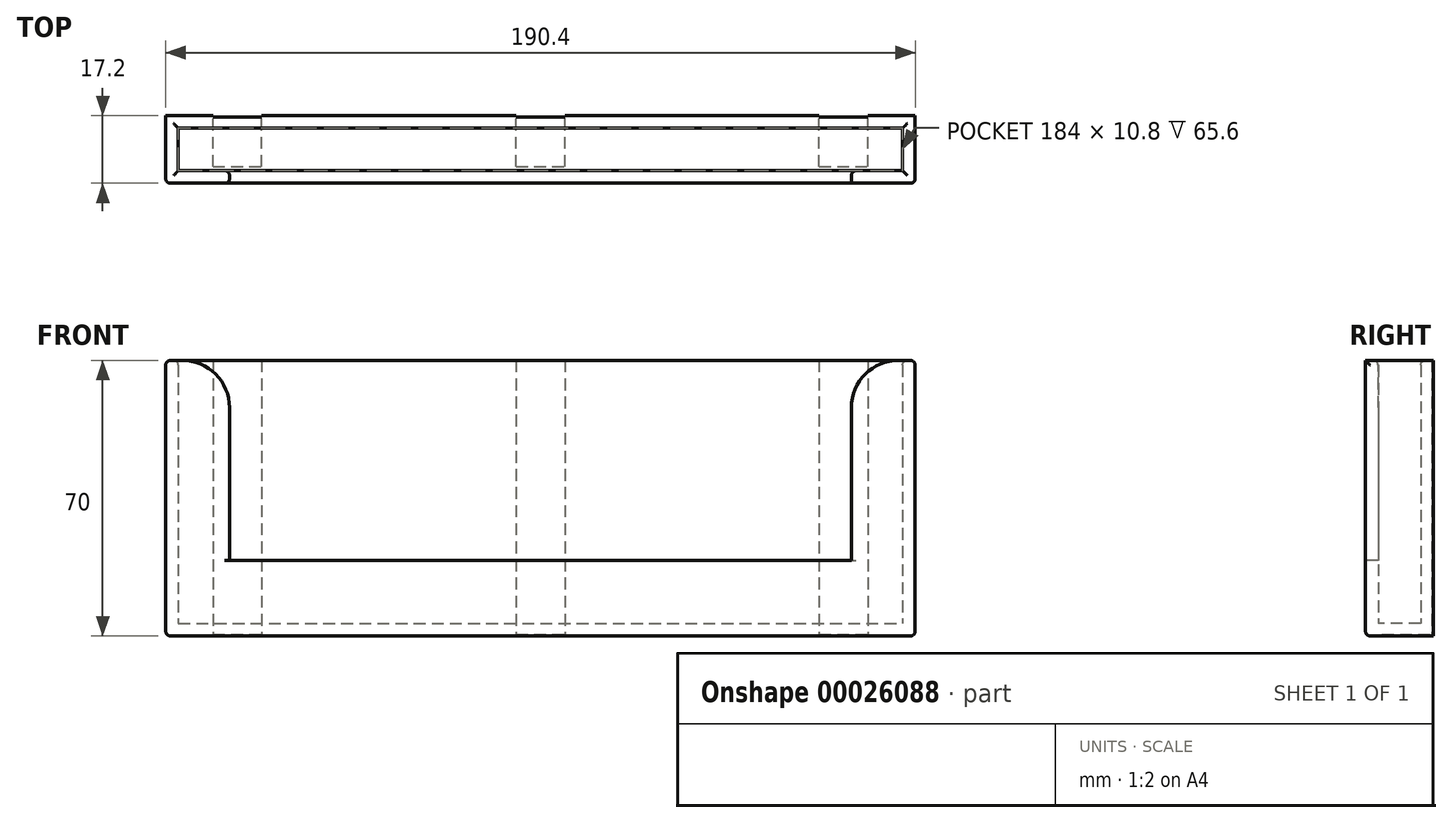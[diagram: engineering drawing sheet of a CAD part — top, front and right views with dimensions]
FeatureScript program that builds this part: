
annotation { "Feature Type Name" : "Feature", "Feature Type Description" : "" }
export const myFeature = defineFeature(function(context is Context, id is Id, definition is map)
    precondition{}
    {
        {
            var Q0;
            Q0=qCreatedBy(makeId("Top.planeOp"),FACE);
            var sketch = newSketch(context, id + "F0", { "sketchPlane" : qUnion([Q0])});
            skLineSegment(sketch, "E0.bottom", {"start": v(-78.63, 21.45) * mm, "end": v(105.37, 21.45) * mm});
            skLineSegment(sketch, "E0.top", {"start": v(-78.63, 10.65) * mm, "end": v(105.37, 10.65) * mm});
            skLineSegment(sketch, "E0.left", {"start": v(-78.63, 21.45) * mm, "end": v(-78.63, 10.65) * mm});
            skLineSegment(sketch, "E0.right", {"start": v(105.37, 21.45) * mm, "end": v(105.37, 10.65) * mm});
            skSolve(sketch);
        }
        {
            var Q0;
            Q0=makeQuery(id+"F0.imprint","IMPRINT",FACE,{"disambiguationData":[TD([[makeQuery(id+"F0.imprint","IMPRINT",EDGE,{"derivedFrom":sQuery(id+"F0.wireOp",EDGE,"E0.bottom")}),-1.0]])]});
            extrude(context, id + "F1", {"entities" : qUnion([Q0]), "depth" : 3.2 * mm});
        }
        {
            var Q0;
            Q0=qCreatedBy(makeId("Top.planeOp"),FACE);
            var sketch = newSketch(context, id + "F2", { "sketchPlane" : qUnion([Q0])});
            skLineSegment(sketch, "E1.0", {"start": v(-78.63, 10.65) * mm, "end": v(105.37, 10.65) * mm});
            skLineSegment(sketch, "E2.0", {"start": v(-78.63, 21.45) * mm, "end": v(-78.63, 10.65) * mm});
            skLineSegment(sketch, "E3.0", {"start": v(-78.63, 21.45) * mm, "end": v(105.37, 21.45) * mm});
            skLineSegment(sketch, "E4.0", {"start": v(105.37, 21.45) * mm, "end": v(105.37, 10.65) * mm});
            skLineSegment(sketch, "E5.0", {"start": v(-81.83, 7.45) * mm, "end": v(108.57, 7.45) * mm});
            skLineSegment(sketch, "E6.0", {"start": v(-81.83, 24.65) * mm, "end": v(108.57, 24.65) * mm});
            skLineSegment(sketch, "E7.0", {"start": v(-81.83, 24.65) * mm, "end": v(-81.83, 7.45) * mm});
            skLineSegment(sketch, "E8.0", {"start": v(108.57, 24.65) * mm, "end": v(108.57, 7.45) * mm});
            skSolve(sketch);
        }
        {
            var Q0;
            Q0=makeQuery(id+"F2.imprint","IMPRINT",FACE,{"disambiguationData":[TD([[makeQuery(id+"F2.imprint","IMPRINT",EDGE,{"derivedFrom":sQuery(id+"F2.wireOp",EDGE,"E1.0")}),-1.0]])]});
            extrude(context, id + "F3", {"entities" : qUnion([Q0]), "operationType" : NewBodyOperationType.ADD, "depth" : 70 * mm});
        }
        {
            var Q0;
            Q0=makeQuery(id+"F3.opExtrude","SWEPT_FACE",FACE,{"disambiguationData":[OSD([sQuery(id+"F2.wireOp",EDGE,"E5.0")])]});
            var sketch = newSketch(context, id + "F4", { "sketchPlane" : qUnion([Q0])});
            skLineSegment(sketch, "E9.0", {"start": v(-65.63, 19.2) * mm, "end": v(92.37, 19.2) * mm});
            skLineSegment(sketch, "E10.0", {"start": v(-65.63, 58) * mm, "end": v(-65.63, 19.2) * mm});
            skLineSegment(sketch, "E11.0", {"start": v(92.37, 58) * mm, "end": v(92.37, 19.2) * mm});
            skLineSegment(sketch, "E12.0", {"start": v(-81.83, 70) * mm, "end": v(-77.63, 70) * mm});
            skLineSegment(sketch, "E13.trimOffspring", {"start": v(104.37, 70) * mm, "end": v(108.57, 70) * mm});
            skPoint(sketch, "E14.visualSharp", {"position": v(-65.63, 70) * mm});
            skArc(sketch, "E14.filletArc", {"start": v(-65.63, 58) * mm, "mid": v(-69.15, 66.49) * mm, "end": v(-77.63, 70) * mm});
            skPoint(sketch, "E15.visualSharp", {"position": v(92.37, 70) * mm});
            skArc(sketch, "E15.filletArc", {"start": v(104.37, 70) * mm, "mid": v(95.88, 66.49) * mm, "end": v(92.37, 58) * mm});
            skSolve(sketch);
        }
        {
            var Q0;
            Q0=makeQuery(id+"F4.imprint","IMPRINT",FACE,{"disambiguationData":[TD([[makeQuery(id+"F4.imprint","IMPRINT",EDGE,{"derivedFrom":sQuery(id+"F4.wireOp",EDGE,"E9.0")}),1.0]])]});
            var Q1;
            Q1=makeQuery(id+"F3.opExtrude","SWEPT_FACE",FACE,{"disambiguationData":[OSD([sQuery(id+"F2.wireOp",EDGE,"E1.0")])]});
            extrude(context, id + "F5", {"entities" : qUnion([Q0]), "operationType" : NewBodyOperationType.REMOVE, "endBound" : BoundingType.UP_TO_SURFACE, "oppositeDirection" : true, "endBoundEntityFace" : qUnion([Q1]), "depth" : 25.4 * mm});
        }
        {
            var Q0;
            Q0=makeQuery(id+"F3.opExtrude","SWEPT_FACE",FACE,{"disambiguationData":[OSD([sQuery(id+"F2.wireOp",EDGE,"E6.0")])]});
            var sketch = newSketch(context, id + "F6", { "sketchPlane" : qUnion([Q0])});
            skLineSegment(sketch, "E16.0", {"start": v(-108.57, 70) * mm, "end": v(-108.57, 0) * mm});
            skLineSegment(sketch, "E17.0", {"start": v(81.83, 0) * mm, "end": v(-108.57, 0) * mm});
            skLineSegment(sketch, "E18.0", {"start": v(81.83, 70) * mm, "end": v(81.83, 0) * mm});
            skLineSegment(sketch, "E19.0", {"start": v(81.83, 70) * mm, "end": v(-108.57, 70) * mm});
            skLineSegment(sketch, "E20", {"start": v(-13.37, 70) * mm, "end": v(-13.37, 0) * mm, "construction": true});
            skLineSegment(sketch, "E21.0", {"start": v(-19.57, 70) * mm, "end": v(-19.57, 0) * mm});
            skLineSegment(sketch, "E22.0", {"start": v(-7.17, 70) * mm, "end": v(-7.17, 0) * mm});
            skLineSegment(sketch, "E23.0", {"start": v(-96.57, 70) * mm, "end": v(-96.57, 0) * mm});
            skLineSegment(sketch, "E24.0", {"start": v(-84.17, 70) * mm, "end": v(-84.17, 0) * mm});
            skLineSegment(sketch, "E25.0", {"start": v(69.83, 70) * mm, "end": v(69.83, 0) * mm});
            skLineSegment(sketch, "E26.0", {"start": v(57.43, 70) * mm, "end": v(57.43, 0) * mm});
            skSolve(sketch);
        }
        {
            var Q0;
            {var subQ0=sQuery(id+"F6.wireOp",EDGE,"E23.0");Q0=makeQuery(id+"F6.imprint","IMPRINT",FACE,{"disambiguationData":[TD([[makeQuery(id+"F6.imprint","IMPRINT",EDGE,{"derivedFrom":subQ0}),1.0]])]});}
            var Q1;
            {var subQ0=sQuery(id+"F6.wireOp",EDGE,"E21.0");Q1=makeQuery(id+"F6.imprint","IMPRINT",FACE,{"disambiguationData":[TD([[makeQuery(id+"F6.imprint","IMPRINT",EDGE,{"derivedFrom":subQ0}),1.0]])]});}
            var Q2;
            {var subQ0=sQuery(id+"F6.wireOp",EDGE,"E25.0");Q2=makeQuery(id+"F6.imprint","IMPRINT",FACE,{"disambiguationData":[TD([[makeQuery(id+"F6.imprint","IMPRINT",EDGE,{"derivedFrom":subQ0}),-1.0]])]});}
            extrude(context, id + "F7", {"entities" : qUnion([Q0, Q1, Q2]), "operationType" : NewBodyOperationType.REMOVE, "oppositeDirection" : true, "depth" : .4 * mm});
        }
        {
            var Q0;
            Q0=makeQuery(id+"F3.boolean.opBoolean","MERGE",FACE,{"derivedFrom":[makeQuery(id+"F1.opExtrude","CAP_FACE",FACE,{"disambiguationData":[OSD([sQuery(id+"F0.wireOp",EDGE,"E0.bottom"),sQuery(id+"F0.wireOp",EDGE,"E0.top"),sQuery(id+"F0.wireOp",EDGE,"E0.left"),sQuery(id+"F0.wireOp",EDGE,"E0.right")])],"isStart":true}),makeQuery(id+"F3.opExtrude","CAP_FACE",FACE,{"disambiguationData":[OSD([sQuery(id+"F2.wireOp",EDGE,"E1.0"),sQuery(id+"F2.wireOp",EDGE,"E2.0"),sQuery(id+"F2.wireOp",EDGE,"E3.0"),sQuery(id+"F2.wireOp",EDGE,"E4.0"),sQuery(id+"F2.wireOp",EDGE,"E5.0"),sQuery(id+"F2.wireOp",EDGE,"E6.0"),sQuery(id+"F2.wireOp",EDGE,"E7.0"),sQuery(id+"F2.wireOp",EDGE,"E8.0")])],"isStart":true})]});
            var sketch = newSketch(context, id + "F8", { "sketchPlane" : qUnion([Q0])});
            skLineSegment(sketch, "E27.0", {"start": v(96.57, -24.65) * mm, "end": v(108.57, -24.65) * mm, "construction": true});
            skLineSegment(sketch, "E28.0", {"start": v(108.57, -24.65) * mm, "end": v(108.57, -7.45) * mm, "construction": true});
            skLineSegment(sketch, "E29.0", {"start": v(84.17, -24.25) * mm, "end": v(96.57, -24.25) * mm});
            skLineSegment(sketch, "E30.0", {"start": v(96.57, -11.65) * mm, "end": v(96.57, -24.65) * mm});
            skLineSegment(sketch, "E31.0", {"start": v(84.17, -11.65) * mm, "end": v(84.17, -24.65) * mm});
            skLineSegment(sketch, "E32.0", {"start": v(19.57, -24.65) * mm, "end": v(84.17, -24.65) * mm, "construction": true});
            skLineSegment(sketch, "E33.0", {"start": v(19.57, -11.65) * mm, "end": v(19.57, -24.65) * mm});
            skLineSegment(sketch, "E34.0", {"start": v(7.17, -24.25) * mm, "end": v(19.57, -24.25) * mm});
            skLineSegment(sketch, "E35.0", {"start": v(7.17, -11.65) * mm, "end": v(7.17, -24.65) * mm});
            skLineSegment(sketch, "E36.0", {"start": v(-57.43, -24.65) * mm, "end": v(7.17, -24.65) * mm, "construction": true});
            skLineSegment(sketch, "E37.0", {"start": v(-57.43, -11.65) * mm, "end": v(-57.43, -24.65) * mm});
            skLineSegment(sketch, "E38.0", {"start": v(-69.83, -24.25) * mm, "end": v(-57.43, -24.25) * mm});
            skLineSegment(sketch, "E39.0", {"start": v(-69.83, -11.65) * mm, "end": v(-69.83, -24.65) * mm});
            skLineSegment(sketch, "E40.0", {"start": v(-81.83, -24.65) * mm, "end": v(-69.83, -24.65) * mm, "construction": true});
            skLineSegment(sketch, "E41.0", {"start": v(-81.83, -24.65) * mm, "end": v(-81.83, -7.45) * mm, "construction": true});
            skLineSegment(sketch, "E42.0", {"start": v(-69.83, -11.65) * mm, "end": v(-57.43, -11.65) * mm});
            skLineSegment(sketch, "E43.trimOffspring", {"start": v(84.17, -11.65) * mm, "end": v(96.57, -11.65) * mm});
            skLineSegment(sketch, "E44.trimOffspring", {"start": v(7.17, -11.65) * mm, "end": v(19.57, -11.65) * mm});
            skSolve(sketch);
        }
        {
            var Q0;
            {var subQ0=sQuery(id+"F8.wireOp",EDGE,"E34.0");Q0=makeQuery(id+"F8.imprint","IMPRINT",FACE,{"disambiguationData":[TD([[makeQuery(id+"F8.imprint","IMPRINT",EDGE,{"derivedFrom":subQ0}),1.0]])]});}
            var Q1;
            {var subQ0=sQuery(id+"F8.wireOp",EDGE,"E38.0");Q1=makeQuery(id+"F8.imprint","IMPRINT",FACE,{"disambiguationData":[TD([[makeQuery(id+"F8.imprint","IMPRINT",EDGE,{"derivedFrom":subQ0}),1.0]])]});}
            var Q2;
            {var subQ0=sQuery(id+"F8.wireOp",EDGE,"E29.0");Q2=makeQuery(id+"F8.imprint","IMPRINT",FACE,{"disambiguationData":[TD([[makeQuery(id+"F8.imprint","IMPRINT",EDGE,{"derivedFrom":subQ0}),1.0]])]});}
            extrude(context, id + "F9", {"entities" : qUnion([Q0, Q1, Q2]), "operationType" : NewBodyOperationType.REMOVE, "oppositeDirection" : true, "depth" : .4 * mm});
        }
        {
            var Q0;
            Q0=makeQuery(id+"F3.opExtrude","SWEPT_EDGE",EDGE,{"disambiguationData":[OSD([sQuery(id+"F2.wireOp",EDGE,"E5.0"),sQuery(id+"F2.wireOp",EDGE,"E7.0")])]});
            var Q1;
            {var subQ0=sQuery(id+"F2.wireOp",EDGE,"E7.0");var subQ1=sQuery(id+"F2.wireOp",EDGE,"E5.0");Q1=makeQuery(id+"F5.boolean.opBoolean","SPLIT",EDGE,{"disambiguationData":[TD([makeQuery(id+"F3.opExtrude","SWEPT_FACE",FACE,{"disambiguationData":[OSD([subQ0])]})])],"derivedFrom":makeQuery(id+"F3.opExtrude","CAP_EDGE",EDGE,{"disambiguationData":[OSD([subQ1])],"isStart":false})});}
            var Q2;
            Q2=makeQuery(id+"F5.boolean.opBoolean","COPY",EDGE,{"derivedFrom":makeQuery(id+"F5.opExtrude","CAP_EDGE",EDGE,{"disambiguationData":[OSD([sQuery(id+"F4.wireOp",EDGE,"E9.0")])],"isStart":true})});
            var Q3;
            Q3=makeQuery(id+"F5.boolean.opBoolean","COPY",EDGE,{"derivedFrom":makeQuery(id+"F5.opExtrude","CAP_EDGE",EDGE,{"disambiguationData":[OSD([sQuery(id+"F4.wireOp",EDGE,"E11.0")])],"isStart":true})});
            var Q4;
            Q4=makeQuery(id+"F3.opExtrude","SWEPT_EDGE",EDGE,{"disambiguationData":[OSD([sQuery(id+"F2.wireOp",EDGE,"E5.0"),sQuery(id+"F2.wireOp",EDGE,"E8.0")])]});
            var Q5;
            Q5=makeQuery(id+"F3.opExtrude","CAP_EDGE",EDGE,{"disambiguationData":[OSD([sQuery(id+"F2.wireOp",EDGE,"E5.0")])],"isStart":true});
            var Q6;
            Q6=makeQuery(id+"F3.opExtrude","CAP_EDGE",EDGE,{"disambiguationData":[OSD([sQuery(id+"F2.wireOp",EDGE,"E2.0")])],"isStart":false});
            var Q7;
            Q7=makeQuery(id+"F3.opExtrude","CAP_EDGE",EDGE,{"disambiguationData":[OSD([sQuery(id+"F2.wireOp",EDGE,"E3.0")])],"isStart":false});
            var Q8;
            {var subQ0=sQuery(id+"F2.wireOp",EDGE,"E1.0");var subQ1=sQuery(id+"F2.wireOp",EDGE,"E2.0");Q8=makeQuery(id+"F5.boolean.opBoolean","SPLIT",EDGE,{"disambiguationData":[TD([makeQuery(id+"F3.opExtrude","SWEPT_FACE",FACE,{"disambiguationData":[OSD([subQ1])]})])],"derivedFrom":makeQuery(id+"F3.opExtrude","CAP_EDGE",EDGE,{"disambiguationData":[OSD([subQ0])],"isStart":false})});}
            var Q9;
            Q9=makeQuery(id+"F3.opExtrude","CAP_EDGE",EDGE,{"disambiguationData":[OSD([sQuery(id+"F2.wireOp",EDGE,"E4.0")])],"isStart":false});
            var Q10;
            {var subQ0=sQuery(id+"F2.wireOp",EDGE,"E1.0");var subQ1=sQuery(id+"F2.wireOp",EDGE,"E4.0");Q10=makeQuery(id+"F5.boolean.opBoolean","SPLIT",EDGE,{"disambiguationData":[TD([makeQuery(id+"F3.opExtrude","SWEPT_FACE",FACE,{"disambiguationData":[OSD([subQ1])]})])],"derivedFrom":makeQuery(id+"F3.opExtrude","CAP_EDGE",EDGE,{"disambiguationData":[OSD([subQ0])],"isStart":false})});}
            var Q11;
            Q11=makeQuery(id+"F5.boolean.opBoolean","COPY",EDGE,{"derivedFrom":makeQuery(id+"F5.opExtrude","CAP_EDGE",EDGE,{"disambiguationData":[OSD([sQuery(id+"F4.wireOp",EDGE,"E9.0")])],"isStart":false})});
            var Q12;
            Q12=makeQuery(id+"F3.opExtrude","CAP_EDGE",EDGE,{"disambiguationData":[OSD([sQuery(id+"F2.wireOp",EDGE,"E7.0")])],"isStart":true});
            var Q13;
            Q13=makeQuery(id+"F3.opExtrude","CAP_EDGE",EDGE,{"disambiguationData":[OSD([sQuery(id+"F2.wireOp",EDGE,"E8.0")])],"isStart":true});
            var Q14;
            Q14=makeQuery(id+"F3.opExtrude","CAP_EDGE",EDGE,{"disambiguationData":[OSD([sQuery(id+"F2.wireOp",EDGE,"E7.0")])],"isStart":false});
            var Q15;
            Q15=makeQuery(id+"F3.opExtrude","CAP_EDGE",EDGE,{"disambiguationData":[OSD([sQuery(id+"F2.wireOp",EDGE,"E8.0")])],"isStart":false});
            var Q16;
            Q16=makeQuery(id+"F9.boolean.opBoolean","COPY",EDGE,{"derivedFrom":makeQuery(id+"F9.opExtrude","CAP_EDGE",EDGE,{"disambiguationData":[OSD([sQuery(id+"F8.wireOp",EDGE,"E29.0")])],"isStart":false})});
            var Q17;
            Q17=makeQuery(id+"F9.boolean.opBoolean","COPY",EDGE,{"derivedFrom":makeQuery(id+"F9.opExtrude","CAP_EDGE",EDGE,{"disambiguationData":[OSD([sQuery(id+"F8.wireOp",EDGE,"E34.0")])],"isStart":false})});
            var Q18;
            Q18=makeQuery(id+"F9.boolean.opBoolean","COPY",EDGE,{"derivedFrom":makeQuery(id+"F9.opExtrude","CAP_EDGE",EDGE,{"disambiguationData":[OSD([sQuery(id+"F8.wireOp",EDGE,"E38.0")])],"isStart":false})});
            fillet(context, id + "F10", {"entities" : qUnion([Q0, Q1, Q2, Q3, Q4, Q5, Q6, Q7, Q8, Q9, Q10, Q11, Q12, Q13, Q14, Q15, Q16, Q17, Q18]), "radius" : 1.2 * mm, "tangentPropagation" : true, "allowEdgeOverflow" : false});
        }
    });
